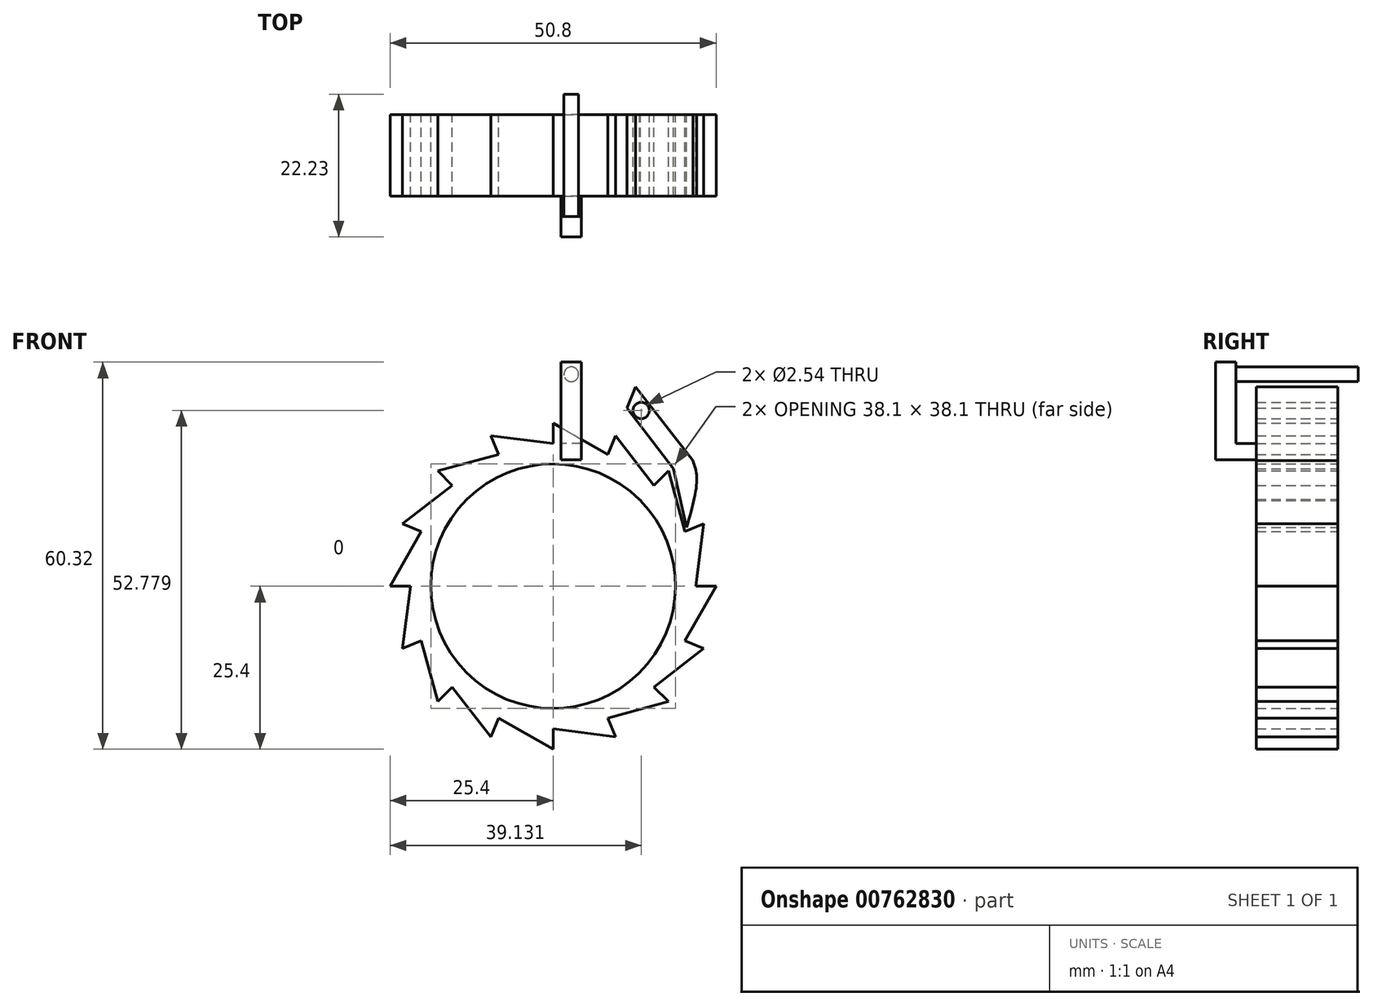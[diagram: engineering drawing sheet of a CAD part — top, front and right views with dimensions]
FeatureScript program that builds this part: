
annotation { "Feature Type Name" : "Feature", "Feature Type Description" : "" }
export const myFeature = defineFeature(function(context is Context, id is Id, definition is map)
    precondition{}
    {
        {
            var Q0;
            Q0=qCreatedBy(makeId("Front.planeOp"),FACE);
            var sketch = newSketch(context, id + "F0", { "sketchPlane" : qUnion([Q0])});
            skCircle(sketch, "E0", {"center": v(0, 0) * mm, "radius": 19.05 * mm});
            skLineSegment(sketch, "E1", {"start": v(0, 25.4) * mm, "end": v(0, -25.4) * mm});
            skLineSegment(sketch, "E2", {"start": v(25.4, 0) * mm, "end": v(-25.4, 0) * mm});
            skLineSegment(sketch, "E3", {"start": v(0, 0) * mm, "end": v(17.96, -17.96) * mm});
            skLineSegment(sketch, "E4", {"start": v(0, 0) * mm, "end": v(-17.96, 17.96) * mm});
            skLineSegment(sketch, "E5", {"start": v(0, 0) * mm, "end": v(17.96, 17.96) * mm});
            skLineSegment(sketch, "E6", {"start": v(0, 0) * mm, "end": v(-17.96, -17.96) * mm});
            skLineSegment(sketch, "E7", {"start": v(0, 0) * mm, "end": v(23.47, 9.72) * mm});
            skLineSegment(sketch, "E8", {"start": v(0, 0) * mm, "end": v(-9.72, 23.47) * mm});
            skLineSegment(sketch, "E9", {"start": v(0, 0) * mm, "end": v(9.72, 23.47) * mm});
            skLineSegment(sketch, "E10", {"start": v(0, 0) * mm, "end": v(-23.47, 9.72) * mm});
            skLineSegment(sketch, "E11", {"start": v(0, 0) * mm, "end": v(-23.47, -9.72) * mm});
            skLineSegment(sketch, "E12", {"start": v(0, 0) * mm, "end": v(-9.72, -23.47) * mm});
            skLineSegment(sketch, "E13", {"start": v(0, 0) * mm, "end": v(9.72, -23.47) * mm});
            skLineSegment(sketch, "E14", {"start": v(0, 0) * mm, "end": v(23.47, -9.72) * mm});
            skLineSegment(sketch, "E15", {"start": v(13.6, 13.34) * mm, "end": v(13.53, 13.53) * mm});
            skCircle(sketch, "E16", {"center": v(0, 0) * mm, "radius": 22.23 * mm});
            skFitSpline(sketch, "E17", {"points": [v(-17.96, 17.96) * mm, v(-8.5, 20.53) * mm], "startDerivative": vector(9.46, 2.57) * mm, "endDerivative": vector(9.46, 2.57) * mm});
            skPoint(sketch, "E18.orphan", {"position": v(0, 19.05) * mm});
            skPoint(sketch, "E19.orphan", {"position": v(19.05, 0) * mm});
            skFitSpline(sketch, "E20", {"points": [v(-9.72, 23.47) * mm, v(0, 22.23) * mm], "startDerivative": vector(9.72, -1.24) * mm, "endDerivative": vector(9.72, -1.24) * mm});
            skFitSpline(sketch, "E21", {"points": [v(0, 25.4) * mm, v(8.5, 20.53) * mm], "startDerivative": vector(8.5, -4.87) * mm, "endDerivative": vector(8.5, -4.87) * mm});
            skFitSpline(sketch, "E22", {"points": [v(9.72, 23.47) * mm, v(15.72, 15.72) * mm], "startDerivative": vector(6, -7.75) * mm, "endDerivative": vector(6, -7.75) * mm});
            skFitSpline(sketch, "E23", {"points": [v(17.96, 17.96) * mm, v(20.53, 8.5) * mm], "startDerivative": vector(2.57, -9.46) * mm, "endDerivative": vector(2.57, -9.46) * mm});
            skFitSpline(sketch, "E24", {"points": [v(23.47, 9.72) * mm, v(22.23, 0) * mm], "startDerivative": vector(-1.24, -9.72) * mm, "endDerivative": vector(-1.24, -9.72) * mm});
            skFitSpline(sketch, "E25", {"points": [v(25.4, 0) * mm, v(20.53, -8.5) * mm], "startDerivative": vector(-4.87, -8.5) * mm, "endDerivative": vector(-4.87, -8.5) * mm});
            skFitSpline(sketch, "E26", {"points": [v(23.47, -9.72) * mm, v(15.72, -15.72) * mm], "startDerivative": vector(-7.75, -6) * mm, "endDerivative": vector(-7.75, -6) * mm});
            skFitSpline(sketch, "E27", {"points": [v(17.96, -17.96) * mm, v(8.5, -20.53) * mm], "startDerivative": vector(-9.46, -2.57) * mm, "endDerivative": vector(-9.46, -2.57) * mm});
            skFitSpline(sketch, "E28", {"points": [v(9.72, -23.47) * mm, v(0, -22.23) * mm], "startDerivative": vector(-9.72, 1.24) * mm, "endDerivative": vector(-9.72, 1.24) * mm});
            skFitSpline(sketch, "E29", {"points": [v(0, -25.4) * mm, v(-8.5, -20.53) * mm], "startDerivative": vector(-8.5, 4.87) * mm, "endDerivative": vector(-8.5, 4.87) * mm});
            skFitSpline(sketch, "E30", {"points": [v(-9.72, -23.47) * mm, v(-15.72, -15.72) * mm], "startDerivative": vector(-6, 7.75) * mm, "endDerivative": vector(-6, 7.75) * mm});
            skFitSpline(sketch, "E31", {"points": [v(-17.96, -17.96) * mm, v(-20.53, -8.5) * mm], "startDerivative": vector(-2.57, 9.46) * mm, "endDerivative": vector(-2.57, 9.46) * mm});
            skFitSpline(sketch, "E32", {"points": [v(-23.47, -9.72) * mm, v(-22.23, 0) * mm], "startDerivative": vector(1.24, 9.72) * mm, "endDerivative": vector(1.24, 9.72) * mm});
            skFitSpline(sketch, "E33", {"points": [v(-25.4, 0) * mm, v(-20.53, 8.5) * mm], "startDerivative": vector(4.87, 8.5) * mm, "endDerivative": vector(4.87, 8.5) * mm});
            skFitSpline(sketch, "E34", {"points": [v(-23.47, 9.72) * mm, v(-15.72, 15.72) * mm], "startDerivative": vector(7.75, 6) * mm, "endDerivative": vector(7.75, 6) * mm});
            skLineSegment(sketch, "E35", {"start": v(18.76, 18.3) * mm, "end": v(20.8, 9.13) * mm});
            skLineSegment(sketch, "E36", {"start": v(18.76, 18.3) * mm, "end": v(21.77, 19.55) * mm});
            skPoint(sketch, "E37", {"position": v(22.4, 16.62) * mm});
            skFitSpline(sketch, "E38", {"points": [v(20.8, 9.13) * mm, v(22.4, 16.62) * mm, v(21.77, 19.55) * mm], "startDerivative": vector(3.9, 13.57) * mm, "endDerivative": vector(-2.43, 6.73) * mm});
            skPoint(sketch, "E39.end.orphan", {"position": v(23.02, 13.7) * mm});
            skLineSegment(sketch, "E40", {"start": v(10.08, 16.16) * mm, "end": v(12.15, 20.33) * mm});
            skLineSegment(sketch, "E41", {"start": v(14.13, 24.3) * mm, "end": v(18.76, 18.3) * mm});
            skLineSegment(sketch, "E42", {"start": v(14.13, 24.3) * mm, "end": v(11.49, 27.73) * mm});
            skLineSegment(sketch, "E43", {"start": v(11.49, 27.73) * mm, "end": v(12.86, 31.05) * mm});
            skLineSegment(sketch, "E44", {"start": v(21.77, 19.55) * mm, "end": v(12.86, 31.05) * mm});
            skPoint(sketch, "E45.orphan", {"position": v(14.23, 34.36) * mm});
            skLineSegment(sketch, "E46", {"start": v(12.17, 29.39) * mm, "end": v(13.73, 27.38) * mm});
            skCircle(sketch, "E47", {"center": v(13.73, 27.38) * mm, "radius": 1.27 * mm});
            skSolve(sketch);
        }
        {
            var Q0;
            Q0 = qSketchRegion(id + "F0", true);
            extrude(context, id + "F1", {"entities" : qUnion([Q0]), "depth" : 12.7 * mm, "offsetDistance" : 25.4 * mm});
        }
        {
            var Q0;
            Q0 = qSketchRegion(id + "F0", true);
            extrude(context, id + "F2", {"entities" : qUnion([Q0]), "depth" : 12.7 * mm, "offsetDistance" : 25.4 * mm});
        }
        {
            var Q0;
            Q0=makeQuery(id+"F1.opExtrude","CAP_FACE",FACE,{"disambiguationData":[OSD([sQuery(id+"F0.wireOp",EDGE,"E0"),sQuery(id+"F0.wireOp",EDGE,"E1"),sQuery(id+"F0.wireOp",EDGE,"E2"),sQuery(id+"F0.wireOp",EDGE,"E3"),sQuery(id+"F0.wireOp",EDGE,"E4"),sQuery(id+"F0.wireOp",EDGE,"E5"),sQuery(id+"F0.wireOp",EDGE,"E6"),sQuery(id+"F0.wireOp",EDGE,"E7"),sQuery(id+"F0.wireOp",EDGE,"E8"),sQuery(id+"F0.wireOp",EDGE,"E9"),sQuery(id+"F0.wireOp",EDGE,"E10"),sQuery(id+"F0.wireOp",EDGE,"E11"),sQuery(id+"F0.wireOp",EDGE,"E12"),sQuery(id+"F0.wireOp",EDGE,"E13"),sQuery(id+"F0.wireOp",EDGE,"E14"),sQuery(id+"F0.wireOp",EDGE,"E15"),sQuery(id+"F0.wireOp",EDGE,"E17"),sQuery(id+"F0.wireOp",EDGE,"E20"),sQuery(id+"F0.wireOp",EDGE,"E21"),sQuery(id+"F0.wireOp",EDGE,"E22"),sQuery(id+"F0.wireOp",EDGE,"E23"),sQuery(id+"F0.wireOp",EDGE,"E24"),sQuery(id+"F0.wireOp",EDGE,"E25"),sQuery(id+"F0.wireOp",EDGE,"E26"),sQuery(id+"F0.wireOp",EDGE,"E27"),sQuery(id+"F0.wireOp",EDGE,"E28"),sQuery(id+"F0.wireOp",EDGE,"E29"),sQuery(id+"F0.wireOp",EDGE,"E30"),sQuery(id+"F0.wireOp",EDGE,"E31"),sQuery(id+"F0.wireOp",EDGE,"E32"),sQuery(id+"F0.wireOp",EDGE,"E33"),sQuery(id+"F0.wireOp",EDGE,"E34")])],"isStart":false});
            var sketch = newSketch(context, id + "F3", { "sketchPlane" : qUnion([Q0])});
            skLineSegment(sketch, "E48.bottom", {"start": v(1.25, 22.23) * mm, "end": v(4.43, 22.23) * mm});
            skLineSegment(sketch, "E48.top", {"start": v(1.25, 19.7) * mm, "end": v(4.43, 19.7) * mm});
            skLineSegment(sketch, "E48.left", {"start": v(1.25, 22.23) * mm, "end": v(1.25, 19.7) * mm});
            skLineSegment(sketch, "E48.right", {"start": v(4.43, 22.23) * mm, "end": v(4.43, 19.7) * mm});
            skSolve(sketch);
        }
        {
            var Q0;
            Q0 = qSketchRegion(id + "F3", true);
            extrude(context, id + "F4", {"entities" : qUnion([Q0]), "depth" : 6.35 * mm, "offsetDistance" : 25.4 * mm});
        }
        {
            var Q0;
            Q0=makeQuery(id+"F4.opExtrude","SWEPT_FACE",FACE,{"disambiguationData":[OSD([sQuery(id+"F3.wireOp",EDGE,"E48.bottom")])]});
            var sketch = newSketch(context, id + "F5", { "sketchPlane" : qUnion([Q0])});
            skLineSegment(sketch, "E49.bottom", {"start": v(4.43, -19.05) * mm, "end": v(1.25, -19.05) * mm});
            skLineSegment(sketch, "E49.top", {"start": v(4.43, -15.88) * mm, "end": v(1.25, -15.88) * mm});
            skLineSegment(sketch, "E49.left", {"start": v(4.43, -19.05) * mm, "end": v(4.43, -15.88) * mm});
            skLineSegment(sketch, "E49.right", {"start": v(1.25, -19.05) * mm, "end": v(1.25, -15.88) * mm});
            skSolve(sketch);
        }
        {
            var Q0;
            Q0 = qSketchRegion(id + "F5", true);
            extrude(context, id + "F6", {"entities" : qUnion([Q0]), "operationType" : NewBodyOperationType.ADD, "depth" : 12.7 * mm, "offsetDistance" : 25.4 * mm});
        }
        {
            var Q0;
            Q0=makeQuery(id+"F6.opExtrude","SWEPT_FACE",FACE,{"disambiguationData":[OSD([sQuery(id+"F5.wireOp",EDGE,"E49.top")])]});
            var sketch = newSketch(context, id + "F7", { "sketchPlane" : qUnion([Q0])});
            skLineSegment(sketch, "E50", {"start": v(-2.84, 34.93) * mm, "end": v(-2.84, 27.3) * mm});
            skLineSegment(sketch, "E51", {"start": v(-2.84, 34.93) * mm, "end": v(-2.84, 33.02) * mm});
            skCircle(sketch, "E52", {"center": v(-2.84, 33.02) * mm, "radius": 1.14 * mm});
            skSolve(sketch);
        }
        {
            var Q0;
            Q0 = qSketchRegion(id + "F7", true);
            extrude(context, id + "F8", {"entities" : qUnion([Q0]), "operationType" : NewBodyOperationType.ADD, "depth" : 19.05 * mm, "offsetDistance" : 25.4 * mm});
        }
    });
